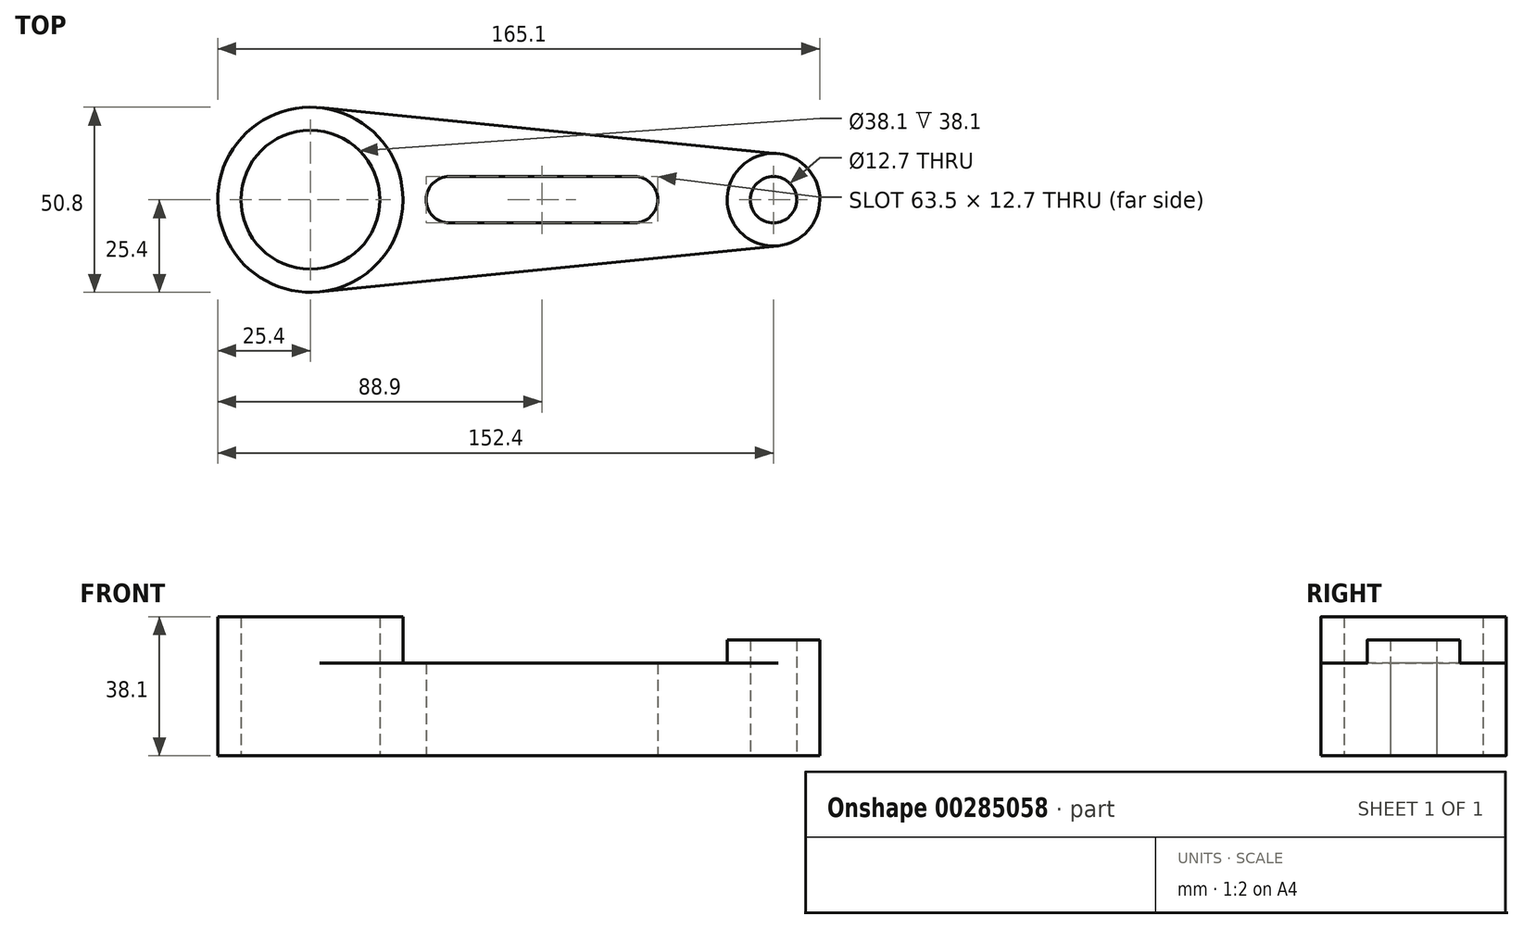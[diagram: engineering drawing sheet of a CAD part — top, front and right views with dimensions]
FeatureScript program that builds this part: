
annotation { "Feature Type Name" : "Feature", "Feature Type Description" : "" }
export const myFeature = defineFeature(function(context is Context, id is Id, definition is map)
    precondition{}
    {
        {
            var Q0;
            Q0=qCreatedBy(makeId("Top.planeOp"),FACE);
            var sketch = newSketch(context, id + "F0", { "sketchPlane" : qUnion([Q0])});
            skCircle(sketch, "E0", {"center": v(0, 0) * mm, "radius": 19.05 * mm});
            skCircle(sketch, "E1", {"center": v(0, 0) * mm, "radius": 25.4 * mm});
            skPoint(sketch, "E2", {"position": v(127, 0) * mm});
            skCircle(sketch, "E3", {"center": v(127, 0) * mm, "radius": 12.7 * mm});
            skCircle(sketch, "E4", {"center": v(127, 0) * mm, "radius": 6.35 * mm});
            skPoint(sketch, "E5", {"position": v(38.1, 0) * mm});
            skPoint(sketch, "E6", {"position": v(88.9, 0) * mm});
            skArc(sketch, "E7", {"start": v(38.1, 6.35) * mm, "mid": v(31.75, 0) * mm, "end": v(38.1, -6.35) * mm});
            skArc(sketch, "E8", {"start": v(88.9, -6.35) * mm, "mid": v(95.25, 0) * mm, "end": v(88.9, 6.35) * mm});
            skPoint(sketch, "E9", {"position": v(38.1, 6.35) * mm});
            skPoint(sketch, "E10", {"position": v(88.9, 6.35) * mm});
            skPoint(sketch, "E11", {"position": v(88.9, -6.35) * mm});
            skPoint(sketch, "E12", {"position": v(38.1, -6.35) * mm});
            skLineSegment(sketch, "E13", {"start": v(38.1, -6.35) * mm, "end": v(88.9, -6.35) * mm});
            skLineSegment(sketch, "E14", {"start": v(38.1, 6.35) * mm, "end": v(88.9, 6.35) * mm});
            skLineSegment(sketch, "E15", {"start": v(2.54, 25.27) * mm, "end": v(128.27, 12.64) * mm});
            skLineSegment(sketch, "E16", {"start": v(2.54, -25.27) * mm, "end": v(128.27, -12.64) * mm});
            skSolve(sketch);
        }
        {
            var Q0;
            Q0=makeQuery(id+"F0.imprint","IMPRINT",FACE,{"disambiguationData":[TD([[makeQuery(id+"F0.imprint","IMPRINT",EDGE,{"derivedFrom":sQuery(id+"F0.wireOp",EDGE,"E0")}),-1.0]])]});
            extrude(context, id + "F1", {"entities" : qUnion([Q0]), "depth" : 38.1 * mm});
        }
        {
            var Q0;
            Q0=makeQuery(id+"F0.imprint","IMPRINT",FACE,{"disambiguationData":[TD([[makeQuery(id+"F0.imprint","IMPRINT",EDGE,{"derivedFrom":sQuery(id+"F0.wireOp",EDGE,"E7")}),-1.0]])]});
            extrude(context, id + "F2", {"entities" : qUnion([Q0]), "operationType" : NewBodyOperationType.ADD, "depth" : 25.4 * mm});
        }
        {
            var Q0;
            Q0=makeQuery(id+"F0.imprint","IMPRINT",FACE,{"disambiguationData":[TD([[makeQuery(id+"F0.imprint","IMPRINT",EDGE,{"derivedFrom":sQuery(id+"F0.wireOp",EDGE,"E4")}),-1.0]])]});
            extrude(context, id + "F3", {"entities" : qUnion([Q0]), "operationType" : NewBodyOperationType.ADD, "depth" : 31.75 * mm});
        }
    });
